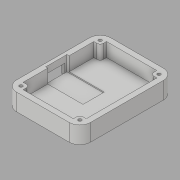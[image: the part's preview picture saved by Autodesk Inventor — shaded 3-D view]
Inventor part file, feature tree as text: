
AUTODESK INVENTOR PART (.ipt)
format: ipt  version: 2019 (Build 230136000, 136)  size: 249,856 bytes
history: native  units: in
note: dims shown in document units (in); Inventor stores cm internally (conversion verified against a paired STEP export)
features: sketch x10, extrude x9, fillet x2, hole x1
ambient origin geometry x8: Origin, YZ Plane, XZ Plane, XY Plane, X Axis, Y Axis, Z Axis, Center Point
bodies: Solid1 (feature_tree)
feature tree (22):
  extrude  "Extrusion1"  Depth=2.7224in
  extrude  "Extrusion2"  Depth=0.1969in
  fillet  "Fillet1"  Radius=0.1969in
  extrude  "Extrusion3"  Depth=0.1969in
  fillet  "Fillet2"  Radius=0.5118in
  hole  "Hole1"  [1 undecoded]
  extrude  "Extrusion4"  Depth=0.2362in
  extrude  "Extrusion5"  Depth=0.2362in
  extrude  "Extrusion6"  Depth=0.2362in
  extrude  "Extrusion7"  Depth=0.5118in TaperAngle=0.0deg
  extrude  "Extrusion11"  Depth=0.2756in
  extrude  "Extrusion12"  Depth=0.2756in
  sketch  "Sketch1"  dims[d0=3.4724in d1=2.7224in]
  sketch  "Sketch2"  dims[d2=0.1181in d3=0.0in d4=0.1969in d5=0.1969in]
  sketch  "Sketch3"  dims[d6=0.1969in d7=0.1969in d8=0.5118in d9=0.0in]
  sketch  "Sketch4"  dims[d10=0.3937in d11=0.2362in]
  sketch  "Sketch5"  dims[d12=0.2362in d13=0.2362in]
  sketch  "Sketch6"  dims[d14=0.2362in d15=0.2362in]
  sketch  "Sketch7"  dims[d16=0.2362in d17=0.2362in]
  sketch  "Sketch8"  dims[d18=0.2362in d19=0.5118in d20=0.0in]
  sketch  "Sketch14"  dims[d21=0.1181in d22=0.2756in]
  sketch  "Sketch15"  dims[d23=0.2756in d24=0.2756in d25=0.2756in d26=0.2756in d27=0.2756in d28=0.2756in d29=0.2756in d30=0.1181in d31=0.2362in d32=0.1575in d33=0.0787in d34=90.0deg d35=0.2362in d36=0.0in d37=0.1575in d38=0.4016in d39=1.1024in d40=1.1024in d41=2.6063in d42=0.5118in d43=0.0in d44=0.1181in d45=0.1181in d46=0.1181in d47=0.1181in d48=0.1181in d49=0.0in d50=0.7874in d51=0.1929in d52=0.1929in d53=0.4016in d54=0.0787in d55=0.0in d56=0.7874in d57=0.7874in d58=1.378in d59=0.0394in d60=0.0in d102=11.811in d103=0.2441in d104=0.2362in d105=0.315in d106=0.2441in d107=0.0394in d108=0.0in d109=0.122in d110=0.122in d111=0.122in d112=0.122in d113=0.1476in d114=0.0394in d115=0.0in]
note: 1 required parameter value undecoded (feature->parameter linkage not recoverable at this tier; creation-order binding heuristic only, values carry confidence <= 0.55)
